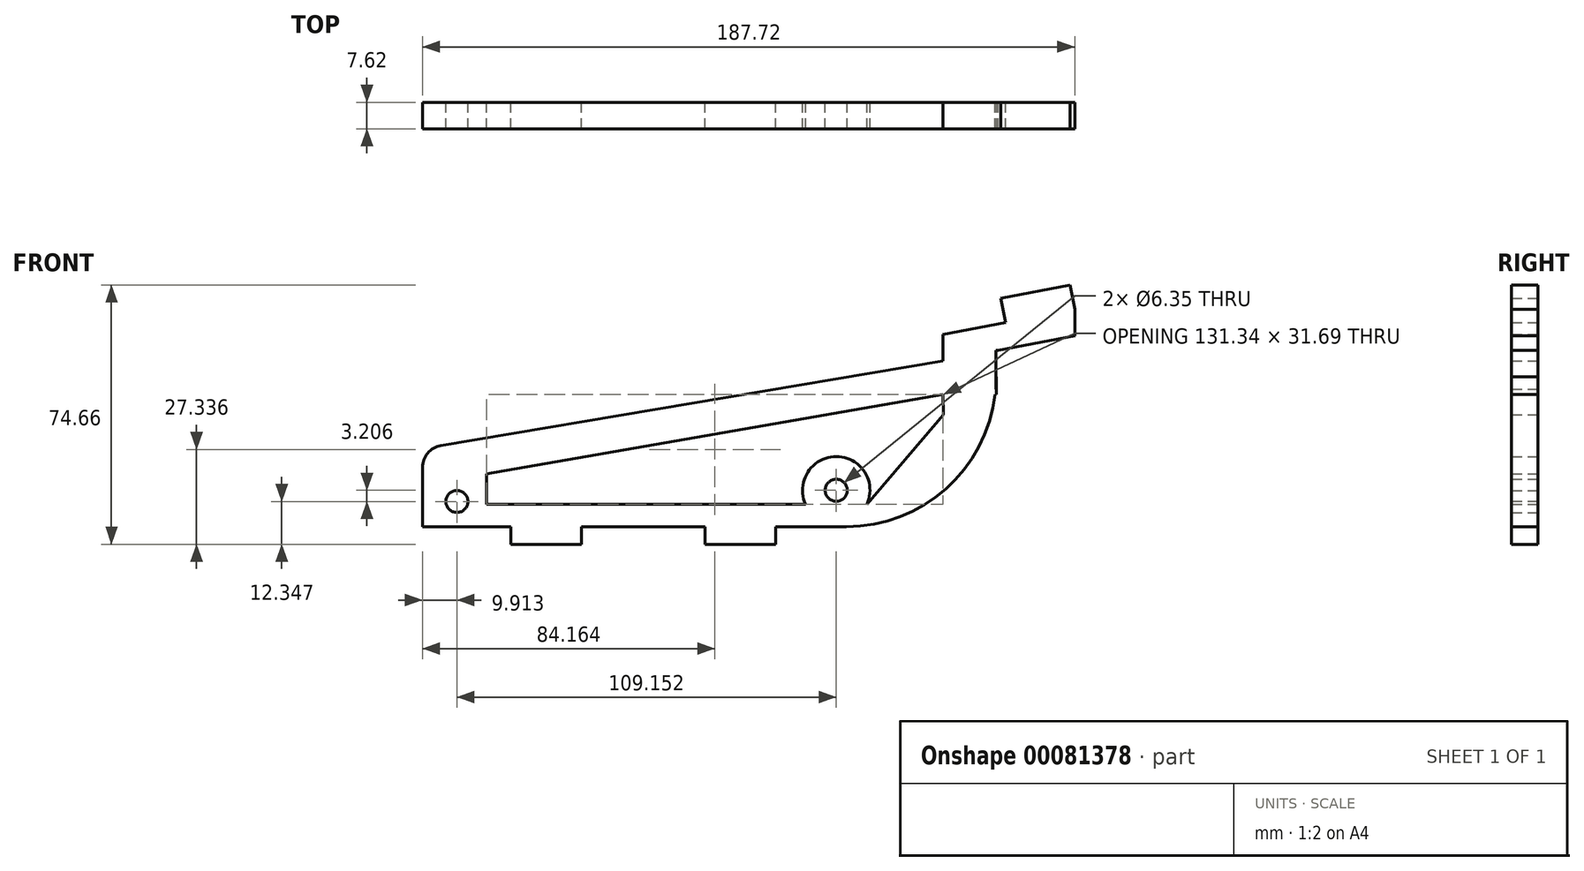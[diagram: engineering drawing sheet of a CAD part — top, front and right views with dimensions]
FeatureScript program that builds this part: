
annotation { "Feature Type Name" : "Feature", "Feature Type Description" : "" }
export const myFeature = defineFeature(function(context is Context, id is Id, definition is map)
    precondition{}
    {
        {
            var Q0;
            Q0=qCreatedBy(makeId("Front.planeOp"),FACE);
            var sketch = newSketch(context, id + "F0", { "sketchPlane" : qUnion([Q0])});
            skLineSegment(sketch, "E0.top", {"start": v(-59.9, -16.75) * mm, "end": v(-24.33, -16.75) * mm});
            skLineSegment(sketch, "E0.right", {"start": v(59.49, 26.42) * mm, "end": v(59.49, 21.35) * mm});
            skPoint(sketch, "E1.visualSharp", {"position": v(59.49, -16.75) * mm});
            skArc(sketch, "E1.filletArc", {"start": v(16.32, -16.75) * mm, "mid": v(46.85, -4.1) * mm, "end": v(59.49, 26.42) * mm});
            skCircle(sketch, "E2", {"center": v(13.45, -6.28) * mm, "radius": 3.18 * mm});
            skLineSegment(sketch, "E3.bottom", {"start": v(59.2, 21.35) * mm, "end": v(59.35, 21.35) * mm});
            skLineSegment(sketch, "E3.top", {"start": v(59.35, 34.05) * mm, "end": v(60.02, 34.05) * mm});
            skLineSegment(sketch, "E3.left", {"start": v(44.1, 21.35) * mm, "end": v(44.1, 31.01) * mm});
            skLineSegment(sketch, "E3.right", {"start": v(59.35, 21.35) * mm, "end": v(59.35, 34.05) * mm});
            skLineSegment(sketch, "E4", {"start": v(-105.61, -16.75) * mm, "end": v(-80.21, -16.75) * mm});
            skLineSegment(sketch, "E5.top", {"start": v(-80.21, -21.83) * mm, "end": v(-59.9, -21.83) * mm});
            skLineSegment(sketch, "E5.left", {"start": v(-80.21, -16.75) * mm, "end": v(-80.21, -21.83) * mm});
            skLineSegment(sketch, "E5.right", {"start": v(-59.9, -16.75) * mm, "end": v(-59.9, -21.83) * mm});
            skLineSegment(sketch, "E6.top", {"start": v(-24.33, -21.83) * mm, "end": v(-4.01, -21.83) * mm});
            skLineSegment(sketch, "E6.left", {"start": v(-24.33, -16.75) * mm, "end": v(-24.33, -21.83) * mm});
            skLineSegment(sketch, "E6.right", {"start": v(-4.01, -16.75) * mm, "end": v(-4.01, -21.83) * mm});
            skLineSegment(sketch, "E7.trimOffspring", {"start": v(-4.01, -16.75) * mm, "end": v(16.32, -16.75) * mm});
            skLineSegment(sketch, "E8.trimOffspring", {"start": v(59.2, 21.35) * mm, "end": v(59.49, 21.35) * mm});
            skLineSegment(sketch, "E9", {"start": v(44.1, 38.63) * mm, "end": v(62.16, 42.08) * mm});
            skLineSegment(sketch, "E10", {"start": v(82.11, 45.89) * mm, "end": v(82.11, 38.27) * mm});
            skLineSegment(sketch, "E11.trimOffspring", {"start": v(60.02, 34.05) * mm, "end": v(82.11, 38.27) * mm});
            skLineSegment(sketch, "E12", {"start": v(44.1, 31.01) * mm, "end": v(44.1, 38.63) * mm});
            skLineSegment(sketch, "E13", {"start": v(82.11, 45.89) * mm, "end": v(80.79, 52.83) * mm});
            skLineSegment(sketch, "E14", {"start": v(80.79, 52.83) * mm, "end": v(60.83, 49.02) * mm});
            skLineSegment(sketch, "E15", {"start": v(60.83, 49.02) * mm, "end": v(62.16, 42.08) * mm});
            skLineSegment(sketch, "E16", {"start": v(22.26, -10.34) * mm, "end": v(44.22, 15.47) * mm});
            skArc(sketch, "E17", {"start": v(22.26, -10.34) * mm, "mid": v(13.45, 3.43) * mm, "end": v(4.65, -10.34) * mm});
            skLineSegment(sketch, "E18", {"start": v(-105.61, -16.75) * mm, "end": v(-105.61, 0.33) * mm});
            skLineSegment(sketch, "E19", {"start": v(44.22, 15.47) * mm, "end": v(44.1, 21.35) * mm});
            skPoint(sketch, "E20.end.orphan", {"position": v(44.1, 27.89) * mm});
            skPoint(sketch, "E20.start.orphan", {"position": v(0, 21.35) * mm});
            skPoint(sketch, "E21.end.orphan", {"position": v(0, 15.47) * mm});
            skLineSegment(sketch, "E22", {"start": v(-100.32, 6.6) * mm, "end": v(44.1, 31.01) * mm});
            skLineSegment(sketch, "E23", {"start": v(44.1, 21.35) * mm, "end": v(-87.12, -1.52) * mm});
            skLineSegment(sketch, "E24", {"start": v(4.65, -10.34) * mm, "end": v(-87.12, -10.34) * mm});
            skLineSegment(sketch, "E25", {"start": v(-87.12, -10.34) * mm, "end": v(-87.12, -1.52) * mm});
            skCircle(sketch, "E26", {"center": v(-95.7, -9.48) * mm, "radius": 3.18 * mm});
            skPoint(sketch, "E27.visualSharp", {"position": v(-105.61, 5.7) * mm});
            skArc(sketch, "E27.filletArc", {"start": v(-100.32, 6.6) * mm, "mid": v(-104.11, 4.43) * mm, "end": v(-105.61, 0.33) * mm});
            skSolve(sketch);
        }
        {
            var Q0;
            Q0 = qSketchRegion(id + "F0", true);
            extrude(context, id + "F1", {"entities" : qUnion([Q0]), "endBound" : BoundingType.SYMMETRIC, "depth" : 7.62 * mm});
        }
    });
